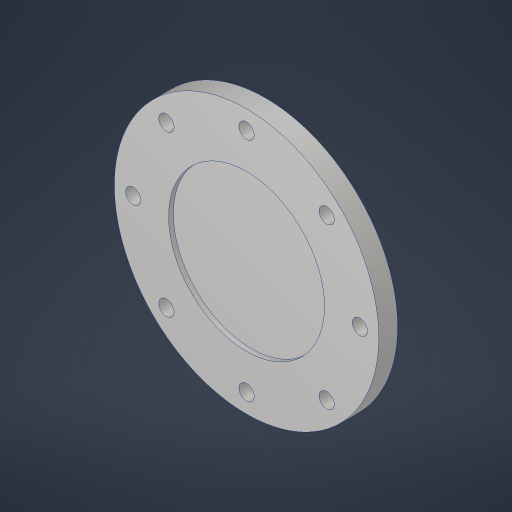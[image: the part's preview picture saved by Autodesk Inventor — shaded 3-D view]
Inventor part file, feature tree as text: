
AUTODESK INVENTOR PART (.ipt)
format: ipt  version: 2023.4 (Build 274418000, 418)  size: 198,144 bytes
history: native  units: in
note: dims shown in document units (in); Inventor stores cm internally (conversion verified against a paired STEP export)
features: sketch x3, extrude x2, hole x1, pattern_circular x1, projected_geometry x1
ambient origin geometry x8: Origin, YZ Plane, XZ Plane, XY Plane, X Axis, Y Axis, Z Axis, Center Point
bodies: Solid1 (feature_tree)
feature tree (8):
  extrude  "Extrusion1"  Depth=0.25in TaperAngle=0.0deg
  hole  "Hole1"  [1 undecoded]
  pattern_circular  "Circular Pattern1"  [2 undecoded]
  extrude  "Extrusion2"  Depth=0.0625in TaperAngle=0.0deg
  sketch  "Sketch1"  dims[d0=3.5in d1=0.25in d2=0.0in]
  sketch  "Sketch2"  dims[d3=3.0in]
  sketch  "Sketch3"  dims[d4=0.201in d5=0.75in d6=0.385in d7=0.25in d8=0.5635in d9=1.0in d10=0.8108in d11=3.1496in d12=360.0deg d14=2.0625in d15=0.0625in d16=0.0in]
  projected_geometry  "Project Cut Edges1"
note: 3 required parameter values undecoded (feature->parameter linkage not recoverable at this tier; creation-order binding heuristic only, values carry confidence <= 0.55)
